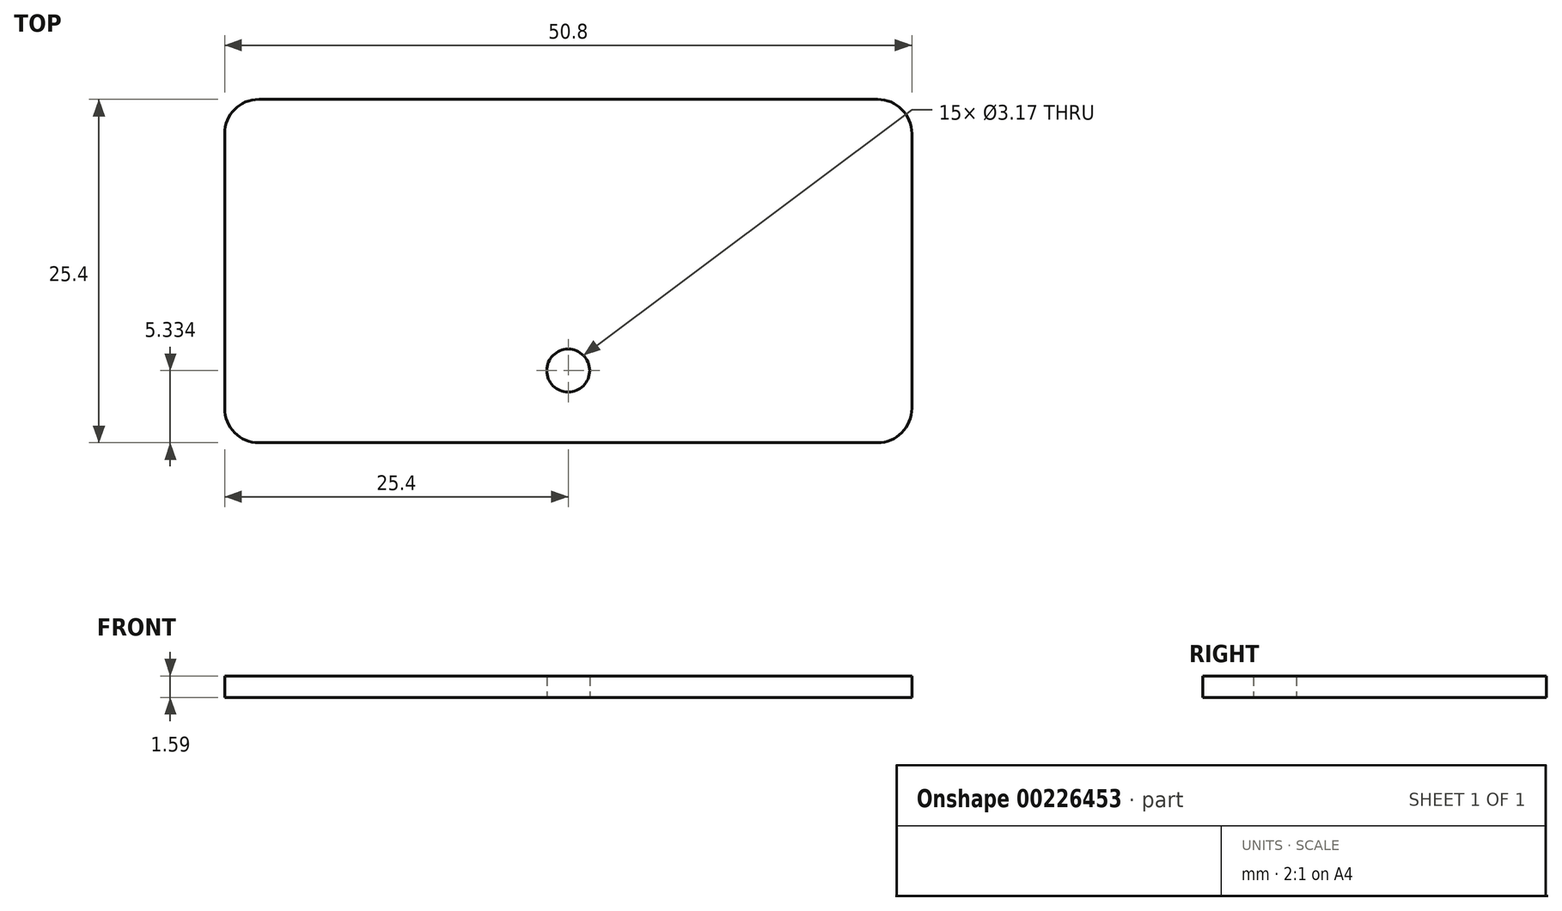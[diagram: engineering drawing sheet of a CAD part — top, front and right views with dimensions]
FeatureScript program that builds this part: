
annotation { "Feature Type Name" : "Feature", "Feature Type Description" : "" }
export const myFeature = defineFeature(function(context is Context, id is Id, definition is map)
    precondition{}
    {
        {
            var Q0;
            Q0=qCreatedBy(makeId("Top.planeOp"),FACE);
            var sketch = newSketch(context, id + "F0", { "sketchPlane" : qUnion([Q0])});
            skLineSegment(sketch, "E0.bottom", {"start": v(22.86, 12.7) * mm, "end": v(-22.86, 12.7) * mm});
            skLineSegment(sketch, "E0.top", {"start": v(22.86, -12.7) * mm, "end": v(-22.86, -12.7) * mm});
            skLineSegment(sketch, "E0.left", {"start": v(25.4, 10.16) * mm, "end": v(25.4, -10.16) * mm});
            skLineSegment(sketch, "E0.right", {"start": v(-25.4, 10.16) * mm, "end": v(-25.4, -10.16) * mm});
            skPoint(sketch, "E0.middle", {"position": v(0, 0) * mm});
            skPoint(sketch, "E1.visualSharp", {"position": v(25.4, 12.7) * mm});
            skArc(sketch, "E1.filletArc", {"start": v(25.4, 10.16) * mm, "mid": v(24.66, 11.96) * mm, "end": v(22.86, 12.7) * mm});
            skPoint(sketch, "E2.visualSharp", {"position": v(25.4, -12.7) * mm});
            skArc(sketch, "E2.filletArc", {"start": v(22.86, -12.7) * mm, "mid": v(24.66, -11.96) * mm, "end": v(25.4, -10.16) * mm});
            skPoint(sketch, "E3.visualSharp", {"position": v(-25.4, -12.7) * mm});
            skArc(sketch, "E3.filletArc", {"start": v(-25.4, -10.16) * mm, "mid": v(-24.66, -11.96) * mm, "end": v(-22.86, -12.7) * mm});
            skPoint(sketch, "E4.visualSharp", {"position": v(-25.4, 12.7) * mm});
            skArc(sketch, "E4.filletArc", {"start": v(-22.86, 12.7) * mm, "mid": v(-24.66, 11.96) * mm, "end": v(-25.4, 10.16) * mm});
            skCircle(sketch, "E5", {"center": v(0, -7.37) * mm, "radius": 1.59 * mm});
            skSolve(sketch);
        }
        {
            var Q0;
            Q0=qSketchRegion(id+"F0",true);
            extrude(context, id + "F1", {"entities" : qUnion([Q0]), "depth" : 1.59 * mm});
        }
    });
